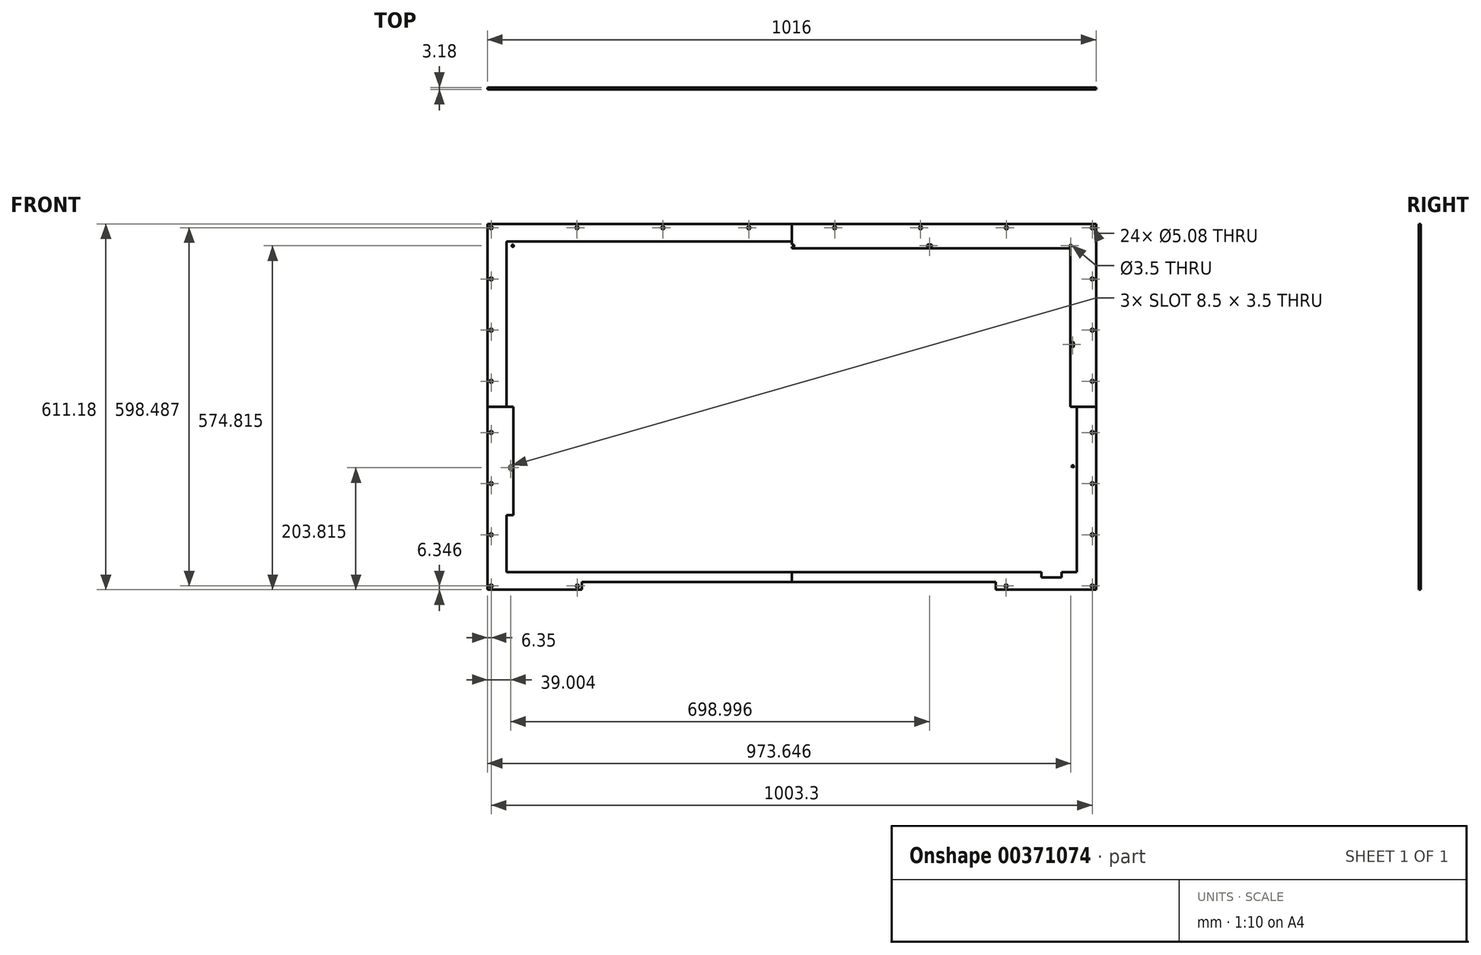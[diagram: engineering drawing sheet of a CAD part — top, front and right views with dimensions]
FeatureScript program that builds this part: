
annotation { "Feature Type Name" : "Feature", "Feature Type Description" : "" }
export const myFeature = defineFeature(function(context is Context, id is Id, definition is map)
    precondition{}
    {
        {
            var Q0;
            Q0=qCreatedBy(makeId("Front.planeOp"),FACE);
            var sketch = newSketch(context, id + "F0", { "sketchPlane" : qUnion([Q0])});
            skLineSegment(sketch, "E0.bottom", {"start": v(495.3, 292.9) * mm, "end": v(-495.3, 292.9) * mm});
            skLineSegment(sketch, "E0.top", {"start": v(495.3, -292.9) * mm, "end": v(-495.3, -292.9) * mm});
            skLineSegment(sketch, "E0.left", {"start": v(495.3, 292.9) * mm, "end": v(495.3, -292.9) * mm});
            skLineSegment(sketch, "E0.right", {"start": v(-495.3, 292.9) * mm, "end": v(-495.3, -292.9) * mm});
            skPoint(sketch, "E0.middle", {"position": v(0, 0) * mm});
            skLineSegment(sketch, "E1.0", {"start": v(-508, 305.6) * mm, "end": v(-508, -305.6) * mm});
            skLineSegment(sketch, "E1.1", {"start": v(508, 305.6) * mm, "end": v(-508, 305.6) * mm});
            skLineSegment(sketch, "E1.2", {"start": v(508, 305.6) * mm, "end": v(508, -305.6) * mm});
            skLineSegment(sketch, "E1.3", {"start": v(508, -305.6) * mm, "end": v(340.3, -305.6) * mm});
            skLineSegment(sketch, "E2.bottom", {"start": v(-476, 276.23) * mm, "end": v(476, 276.23) * mm});
            skLineSegment(sketch, "E2.top", {"start": v(-476, -276.23) * mm, "end": v(476, -276.23) * mm});
            skLineSegment(sketch, "E2.left", {"start": v(-476, 276.23) * mm, "end": v(-476, -276.23) * mm});
            skLineSegment(sketch, "E2.right", {"start": v(476, 276.22) * mm, "end": v(476, -276.23) * mm});
            skLineSegment(sketch, "E3", {"start": v(-508, 305.6) * mm, "end": v(-495.3, 292.9) * mm});
            skPoint(sketch, "E4.middle", {"position": v(-501.65, 299.24) * mm});
            skLineSegment(sketch, "E5.bottom", {"start": v(-464.8, 265.03) * mm, "end": v(464.8, 265.03) * mm});
            skLineSegment(sketch, "E5.top", {"start": v(-464.8, -265.03) * mm, "end": v(464.8, -265.03) * mm});
            skLineSegment(sketch, "E5.left", {"start": v(-464.8, 265.03) * mm, "end": v(-464.8, -265.03) * mm});
            skLineSegment(sketch, "E5.right", {"start": v(464.8, 265.03) * mm, "end": v(464.8, -265.03) * mm});
            skCircle(sketch, "E6", {"center": v(465.65, 269.23) * mm, "radius": 1.75 * mm});
            skCircle(sketch, "E7", {"center": v(0, 269.23) * mm, "radius": 1.75 * mm});
            skLineSegment(sketch, "E8", {"start": v(0, 269.23) * mm, "end": v(0, 276.23) * mm});
            skLineSegment(sketch, "E9", {"start": v(465.65, 269.23) * mm, "end": v(465.65, 276.23) * mm});
            skCircle(sketch, "E10", {"center": v(230, 269.23) * mm, "radius": 1.75 * mm});
            skLineSegment(sketch, "E11", {"start": v(230, 269.23) * mm, "end": v(230, 276.23) * mm});
            skCircle(sketch, "E12.MirrorC", {"center": v(-230, 269.23) * mm, "radius": 1.75 * mm});
            skCircle(sketch, "E13.MirrorC", {"center": v(-465.65, 269.23) * mm, "radius": 1.75 * mm});
            skCircle(sketch, "E14", {"center": v(469, 104.22) * mm, "radius": 1.75 * mm});
            skCircle(sketch, "E15", {"center": v(469, -101.78) * mm, "radius": 1.75 * mm});
            skLineSegment(sketch, "E16", {"start": v(469, -101.78) * mm, "end": v(476, -101.78) * mm});
            skLineSegment(sketch, "E17", {"start": v(469, 104.22) * mm, "end": v(476, 104.22) * mm});
            skCircle(sketch, "E18.MirrorC", {"center": v(-469, -101.78) * mm, "radius": 1.75 * mm});
            skCircle(sketch, "E19.MirrorC", {"center": v(-469, 104.22) * mm, "radius": 1.75 * mm});
            skLineSegment(sketch, "E20", {"start": v(2.5, 269.23) * mm, "end": v(-2.5, 269.23) * mm});
            skArc(sketch, "E21.0.startCap", {"start": v(2.5, 270.98) * mm, "mid": v(4.25, 269.23) * mm, "end": v(2.5, 267.48) * mm});
            skArc(sketch, "E21.0.endCap", {"start": v(-2.5, 267.48) * mm, "mid": v(-4.25, 269.23) * mm, "end": v(-2.5, 270.98) * mm});
            skLineSegment(sketch, "E21.0.left", {"start": v(2.5, 267.48) * mm, "end": v(-2.5, 267.48) * mm});
            skLineSegment(sketch, "E21.0.right", {"start": v(2.5, 270.98) * mm, "end": v(-2.5, 270.98) * mm});
            skLineSegment(sketch, "E22", {"start": v(232.5, 269.22) * mm, "end": v(227.5, 269.22) * mm});
            skArc(sketch, "E23.0.startCap", {"start": v(232.5, 270.97) * mm, "mid": v(234.25, 269.22) * mm, "end": v(232.5, 267.47) * mm});
            skArc(sketch, "E23.0.endCap", {"start": v(227.5, 267.47) * mm, "mid": v(225.75, 269.22) * mm, "end": v(227.5, 270.97) * mm});
            skLineSegment(sketch, "E23.0.left", {"start": v(232.5, 267.47) * mm, "end": v(227.5, 267.47) * mm});
            skLineSegment(sketch, "E23.0.right", {"start": v(232.5, 270.97) * mm, "end": v(227.5, 270.97) * mm});
            skLineSegment(sketch, "E24.MirrorCS", {"start": v(-232.5, 270.97) * mm, "end": v(-227.5, 270.97) * mm});
            skArc(sketch, "E25.MirrorCS", {"start": v(-227.5, 267.47) * mm, "mid": v(-225.75, 269.22) * mm, "end": v(-227.5, 270.97) * mm});
            skLineSegment(sketch, "E26.MirrorCS", {"start": v(-232.5, 267.47) * mm, "end": v(-227.5, 267.47) * mm});
            skArc(sketch, "E27.MirrorCS", {"start": v(-232.5, 270.97) * mm, "mid": v(-234.25, 269.22) * mm, "end": v(-232.5, 267.47) * mm});
            skLineSegment(sketch, "E28", {"start": v(469, 106.72) * mm, "end": v(469, 101.73) * mm});
            skLineSegment(sketch, "E29", {"start": v(469, -99.28) * mm, "end": v(469, -104.27) * mm});
            skArc(sketch, "E30.0.startCap", {"start": v(467.25, 106.72) * mm, "mid": v(469, 108.47) * mm, "end": v(470.75, 106.72) * mm});
            skArc(sketch, "E30.0.endCap", {"start": v(470.75, 101.73) * mm, "mid": v(469, 99.98) * mm, "end": v(467.25, 101.73) * mm});
            skLineSegment(sketch, "E30.0.left", {"start": v(470.75, 106.72) * mm, "end": v(470.75, 101.73) * mm});
            skLineSegment(sketch, "E30.0.right", {"start": v(467.25, 106.72) * mm, "end": v(467.25, 101.73) * mm});
            skArc(sketch, "E30.1.endCap", {"start": v(467.25, -99.28) * mm, "mid": v(469, -97.53) * mm, "end": v(470.75, -99.28) * mm});
            skLineSegment(sketch, "E31.MirrorCS", {"start": v(-470.75, -99.28) * mm, "end": v(-470.75, -104.27) * mm});
            skArc(sketch, "E32.MirrorCS", {"start": v(-467.25, -99.28) * mm, "mid": v(-469, -97.53) * mm, "end": v(-470.75, -99.28) * mm});
            skLineSegment(sketch, "E33.MirrorCS", {"start": v(-467.25, -99.28) * mm, "end": v(-467.25, -104.27) * mm});
            skArc(sketch, "E34.MirrorCS", {"start": v(-470.75, -104.27) * mm, "mid": v(-469, -106.02) * mm, "end": v(-467.25, -104.27) * mm});
            skLineSegment(sketch, "E35.MirrorCS", {"start": v(-470.75, 106.72) * mm, "end": v(-470.75, 101.73) * mm});
            skArc(sketch, "E36.MirrorCS", {"start": v(-467.25, 106.72) * mm, "mid": v(-469, 108.47) * mm, "end": v(-470.75, 106.72) * mm});
            skLineSegment(sketch, "E37.MirrorCS", {"start": v(-467.25, 106.72) * mm, "end": v(-467.25, 101.73) * mm});
            skArc(sketch, "E38.MirrorCS", {"start": v(-470.75, 101.73) * mm, "mid": v(-469, 99.98) * mm, "end": v(-467.25, 101.73) * mm});
            skLineSegment(sketch, "E39", {"start": v(476, -105.78) * mm, "end": v(464.8, -105.78) * mm});
            skLineSegment(sketch, "E40", {"start": v(467.25, -99.28) * mm, "end": v(467.25, -101.78) * mm});
            skLineSegment(sketch, "E41", {"start": v(470.75, -99.28) * mm, "end": v(470.75, -101.78) * mm});
            skLineSegment(sketch, "E42", {"start": v(-464.8, -180.78) * mm, "end": v(-476, -180.78) * mm});
            skLineSegment(sketch, "E43.bottom", {"start": v(450.6, -276.23) * mm, "end": v(416.6, -276.23) * mm});
            skLineSegment(sketch, "E43.top", {"start": v(450.6, -285.23) * mm, "end": v(416.6, -285.23) * mm});
            skLineSegment(sketch, "E43.left", {"start": v(450.6, -276.23) * mm, "end": v(450.6, -285.23) * mm});
            skLineSegment(sketch, "E43.right", {"start": v(416.6, -276.23) * mm, "end": v(416.6, -285.23) * mm});
            skLineSegment(sketch, "E44", {"start": v(340.3, -292.9) * mm, "end": v(340.3, -305.6) * mm});
            skLineSegment(sketch, "E45", {"start": v(-350.3, -292.9) * mm, "end": v(-350.3, -305.6) * mm});
            skLineSegment(sketch, "E46", {"start": v(-495.3, -292.9) * mm, "end": v(-508, -305.6) * mm});
            skPoint(sketch, "E47", {"position": v(-501.65, -299.24) * mm});
            skLineSegment(sketch, "E48.trimOffspring", {"start": v(-350.3, -305.6) * mm, "end": v(-508, -305.6) * mm});
            skCircle(sketch, "E49", {"center": v(-501.65, 299.24) * mm, "radius": 2.54 * mm});
            skCircle(sketch, "E50", {"center": v(-358.32, 299.24) * mm, "radius": 2.54 * mm});
            skCircle(sketch, "E51", {"center": v(-215, 299.24) * mm, "radius": 2.54 * mm});
            skCircle(sketch, "E52", {"center": v(-71.66, 299.24) * mm, "radius": 2.54 * mm});
            skCircle(sketch, "E53", {"center": v(71.66, 299.24) * mm, "radius": 2.54 * mm});
            skCircle(sketch, "E54", {"center": v(215, 299.24) * mm, "radius": 2.54 * mm});
            skCircle(sketch, "E55", {"center": v(-501.65, 213.75) * mm, "radius": 2.54 * mm});
            skCircle(sketch, "E56", {"center": v(-501.65, 128.25) * mm, "radius": 2.54 * mm});
            skCircle(sketch, "E57", {"center": v(-501.65, 42.75) * mm, "radius": 2.54 * mm});
            skCircle(sketch, "E58", {"center": v(-501.65, -42.75) * mm, "radius": 2.54 * mm});
            skCircle(sketch, "E59", {"center": v(358.32, 299.24) * mm, "radius": 2.54 * mm});
            skCircle(sketch, "E60", {"center": v(501.65, 299.24) * mm, "radius": 2.54 * mm});
            skCircle(sketch, "E61", {"center": v(501.65, 213.75) * mm, "radius": 2.54 * mm});
            skCircle(sketch, "E62", {"center": v(501.65, 128.25) * mm, "radius": 2.54 * mm});
            skCircle(sketch, "E63", {"center": v(501.65, 42.75) * mm, "radius": 2.54 * mm});
            skCircle(sketch, "E64", {"center": v(501.65, -42.75) * mm, "radius": 2.54 * mm});
            skCircle(sketch, "E65", {"center": v(501.65, -128.25) * mm, "radius": 2.54 * mm});
            skCircle(sketch, "E66", {"center": v(501.65, -213.75) * mm, "radius": 2.54 * mm});
            skCircle(sketch, "E67", {"center": v(501.65, -299.24) * mm, "radius": 2.54 * mm});
            skCircle(sketch, "E68", {"center": v(357.84, -299.24) * mm, "radius": 2.54 * mm});
            skCircle(sketch, "E69", {"center": v(-357.84, -299.24) * mm, "radius": 2.54 * mm});
            skCircle(sketch, "E70", {"center": v(-501.65, -299.24) * mm, "radius": 2.54 * mm});
            skCircle(sketch, "E71", {"center": v(-501.65, -213.75) * mm, "radius": 2.54 * mm});
            skCircle(sketch, "E72", {"center": v(-501.65, -128.25) * mm, "radius": 2.54 * mm});
            skLineSegment(sketch, "E73", {"start": v(0, 305.6) * mm, "end": v(0, 265.03) * mm});
            skLineSegment(sketch, "E74", {"start": v(0, -265.03) * mm, "end": v(0, -292.9) * mm});
            skLineSegment(sketch, "E75", {"start": v(-464.8, 0) * mm, "end": v(-508, 0) * mm});
            skLineSegment(sketch, "E76", {"start": v(464.8, 0) * mm, "end": v(508, 0) * mm});
            skSolve(sketch);
        }
        {
            var Q0;
            Q0=makeQuery(id+"F0.imprint","IMPRINT",FACE,{"disambiguationData":[TD([[makeQuery(id+"F0.imprint","IMPRINT",EDGE,{"derivedFrom":sQuery(id+"F0.wireOp",EDGE,"E55")}),-1.0]])]});
            var Q1;
            {var subQ0=sQuery(id+"F0.wireOp",EDGE,"E2.left");var subQ1=sQuery(id+"F0.wireOp",EDGE,"E2.bottom");var subQ2=makeQuery(id+"F0.imprint","INTERSECT",VERTEX,{"derivedFrom":[subQ1,subQ0]});Q1=makeQuery(id+"F0.imprint","IMPRINT",FACE,{"disambiguationData":[TD([[makeQuery(id+"F0.imprint","IMPRINT",EDGE,{"disambiguationData":[TD([[subQ2,-1.0]])],"derivedFrom":subQ1}),1.0]])]});}
            var Q2;
            Q2=makeQuery(id+"F0.imprint","IMPRINT",FACE,{"disambiguationData":[TD([[makeQuery(id+"F0.imprint","IMPRINT",EDGE,{"derivedFrom":sQuery(id+"F0.wireOp",EDGE,"E13.MirrorC")}),1.0]])]});
            var Q3;
            Q3=makeQuery(id+"F0.imprint","IMPRINT",FACE,{"disambiguationData":[TD([[makeQuery(id+"F0.imprint","IMPRINT",EDGE,{"derivedFrom":sQuery(id+"F0.wireOp",EDGE,"E50")}),-1.0]])]});
            extrude(context, id + "F1", {"entities" : qUnion([Q0, Q1, Q2, Q3]), "endBound" : BoundingType.SYMMETRIC, "depth" : 3.17 * mm});
        }
        {
            var Q0;
            Q0=makeQuery(id+"F0.imprint","IMPRINT",FACE,{"disambiguationData":[TD([[makeQuery(id+"F0.imprint","IMPRINT",EDGE,{"derivedFrom":sQuery(id+"F0.wireOp",EDGE,"E53")}),-1.0]])]});
            var Q1;
            {var subQ0=sQuery(id+"F0.wireOp",EDGE,"E2.bottom");var subQ1=makeQuery(id+"F0.imprint","IMPRINT",VERTEX,{"disambiguationData":[OD(0.0)],"derivedFrom":subQ0});Q1=makeQuery(id+"F0.imprint","IMPRINT",FACE,{"disambiguationData":[TD([[makeQuery(id+"F0.imprint","IMPRINT",EDGE,{"disambiguationData":[TD([[subQ1,1.0]])],"derivedFrom":subQ0}),1.0]])]});}
            var Q2;
            Q2=makeQuery(id+"F0.imprint","IMPRINT",FACE,{"disambiguationData":[TD([[makeQuery(id+"F0.imprint","IMPRINT",EDGE,{"derivedFrom":sQuery(id+"F0.wireOp",EDGE,"E6")}),-1.0]])]});
            extrude(context, id + "F2", {"entities" : qUnion([Q0, Q1, Q2]), "endBound" : BoundingType.SYMMETRIC, "depth" : 3.17 * mm});
        }
        {
            var Q0;
            Q0=makeQuery(id+"F0.imprint","IMPRINT",FACE,{"disambiguationData":[TD([[makeQuery(id+"F0.imprint","IMPRINT",EDGE,{"derivedFrom":sQuery(id+"F0.wireOp",EDGE,"E43.top")}),1.0]])]});
            var Q1;
            Q1=makeQuery(id+"F0.imprint","IMPRINT",FACE,{"disambiguationData":[TD([[makeQuery(id+"F0.imprint","IMPRINT",EDGE,{"derivedFrom":sQuery(id+"F0.wireOp",EDGE,"E30.1.endCap")}),1.0]])]});
            var Q2;
            {var subQ8=sQuery(id+"F0.wireOp",EDGE,"E1.3");Q2=makeQuery(id+"F0.imprint","IMPRINT",FACE,{"disambiguationData":[TD([[makeQuery(id+"F0.imprint","IMPRINT",EDGE,{"derivedFrom":subQ8}),-1.0]])]});}
            extrude(context, id + "F3", {"entities" : qUnion([Q0, Q1, Q2]), "endBound" : BoundingType.SYMMETRIC, "depth" : 3.17 * mm});
        }
        {
            var Q0;
            {var subQ5=sQuery(id+"F0.wireOp",EDGE,"E0.top");var subQ9=makeQuery(id+"F0.imprint","INTERSECT",VERTEX,{"derivedFrom":[subQ5,sQuery(id+"F0.wireOp",EDGE,"E45")]});Q0=makeQuery(id+"F0.imprint","IMPRINT",FACE,{"disambiguationData":[TD([[makeQuery(id+"F0.imprint","IMPRINT",EDGE,{"disambiguationData":[TD([[subQ9,1.0]])],"derivedFrom":subQ5}),-1.0]])]});}
            var Q1;
            {var subQ8=sQuery(id+"F0.wireOp",EDGE,"E32.MirrorCS");Q1=makeQuery(id+"F0.imprint","IMPRINT",FACE,{"disambiguationData":[TD([[makeQuery(id+"F0.imprint","IMPRINT",EDGE,{"derivedFrom":subQ8}),-1.0]])]});}
            var Q2;
            Q2=makeQuery(id+"F0.imprint","IMPRINT",FACE,{"disambiguationData":[TD([[makeQuery(id+"F0.imprint","IMPRINT",EDGE,{"derivedFrom":sQuery(id+"F0.wireOp",EDGE,"E58")}),-1.0]])]});
            var Q3;
            {var subQ7=sQuery(id+"F0.wireOp",EDGE,"E45");Q3=makeQuery(id+"F0.imprint","IMPRINT",FACE,{"disambiguationData":[TD([[makeQuery(id+"F0.imprint","IMPRINT",EDGE,{"derivedFrom":subQ7}),-1.0]])]});}
            extrude(context, id + "F4", {"entities" : qUnion([Q0, Q1, Q2, Q3]), "endBound" : BoundingType.SYMMETRIC, "depth" : 3.17 * mm});
        }
    });
